# Revit family: Alcon-14130 Large-Revit-Family
name_source: partatom
category: Lighting Fixtures
units: mm (PartAtom-declared; Revit-internal decimal feet)

## family parameters
Always vertical = No
Cut with Voids When Loaded = No
Light Source = No
Maintain Annotation Orientation = No
Part Type = Normal
Room Calculation Point = No
Round Connector Dimension = Use Diameter
Shared = No
Work Plane-Based = Yes

## types (1)
- LTD8321B-B15-T30
    COLOR TEMP = T30: 3000K (90 CRI)
    DIMMING = Blank: 120V 2-Wire/Incandescent/ELV
    Default Elevation = 48"
    Depth = 4 1/8"
    Description = Architecturally styled Cylo Swivel Cylinder LED track head features a durable steel body, futuristic alloy heat sink, hidden wiring and internal adjustment mechanism for a clean unobtrusive look. Its small size makes it ideal for retail, commercial and residential applications requiring stylish design and true PAR20 performance.

Benefits: Standard 90 CRI; Sleek Unabtrusive Design; Concealed heat sink and LED driver; For use with standard H-Style 1 circuit and 2 circuit track; Precision design ensures firm positioning; Highly adjustable, 355º Rotation/0º-90º Gimbal; "Zero Percent Dimming Standard" Smoothly Dims to completely off with Standard ; Incandescent Dimmers; Standard with 2-Wire Incandescent Dimmers and 3-Wire ELV Dimmers.
    Efficacy = 78 lm/W
    FINISH = W: White
    Height = 9 3/16"
    Housing = White
    LED = T30:3000K
    Lamp = LED
    Luminous Flux = 1400 lm
    Manufacturer = ALCON Lighting
    Model = 14130
    Product Page URL = https://www.alconlighting.com
    URL = https://www.alconlighting.com
    Wattage = 18 W
    Width = 3"
    lamp_x = Lamp

## geometry (parser evidence)
native form markers: Sweep x7
no freeform markers — native parametric forms only
